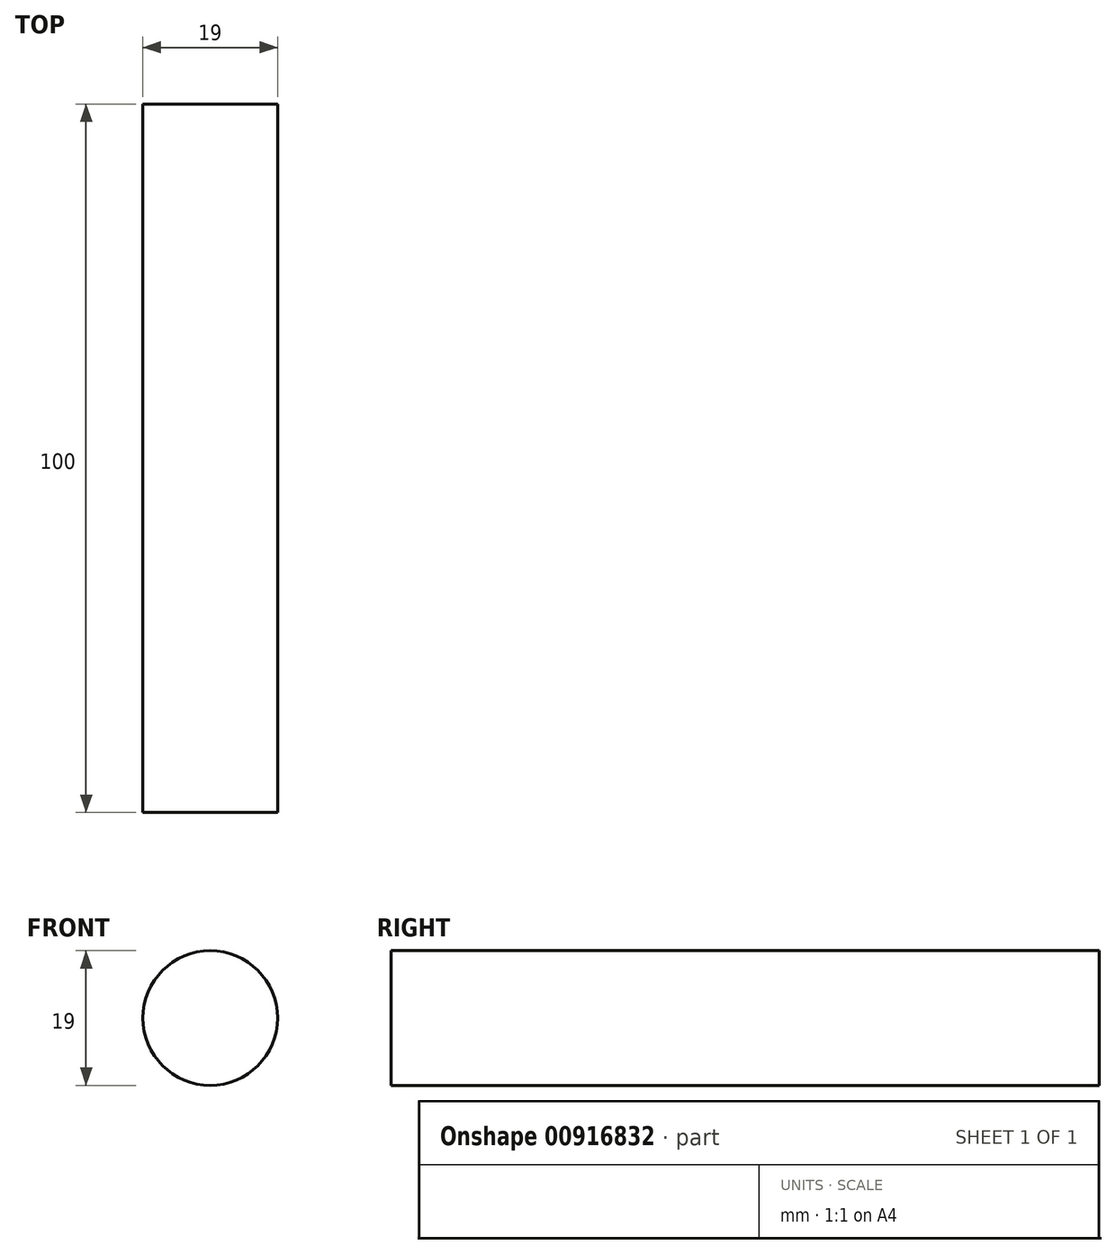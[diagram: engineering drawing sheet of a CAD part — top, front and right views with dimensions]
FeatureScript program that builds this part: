
annotation { "Feature Type Name" : "Feature", "Feature Type Description" : "" }
export const myFeature = defineFeature(function(context is Context, id is Id, definition is map)
    precondition{}
    {
        {
            var Q0;
            Q0=qCreatedBy(makeId("Front.planeOp"),FACE);
            var sketch = newSketch(context, id + "F0", { "sketchPlane" : qUnion([Q0])});
            skCircle(sketch, "E0", {"center": v(0, 0) * mm, "radius": 7 * mm});
            skCircle(sketch, "E1", {"center": v(0, 0) * mm, "radius": 9.5 * mm});
            skSolve(sketch);
        }
        {
            var Q0;
            Q0=makeQuery(id+"F0.imprint","IMPRINT",FACE,{"disambiguationData":[TD([[makeQuery(id+"F0.imprint","IMPRINT",EDGE,{"derivedFrom":sQuery(id+"F0.wireOp",EDGE,"E0")}),-1.0]])]});
            var Q1;
            Q1=makeQuery(id+"F0.imprint","IMPRINT",FACE,{"disambiguationData":[TD([[makeQuery(id+"F0.imprint","IMPRINT",EDGE,{"derivedFrom":sQuery(id+"F0.wireOp",EDGE,"E0")}),1.0]])]});
            extrude(context, id + "F1", {"entities" : qUnion([Q0, Q1]), "depth" : 100 * mm, "offsetDistance" : 25 * mm});
        }
    });
